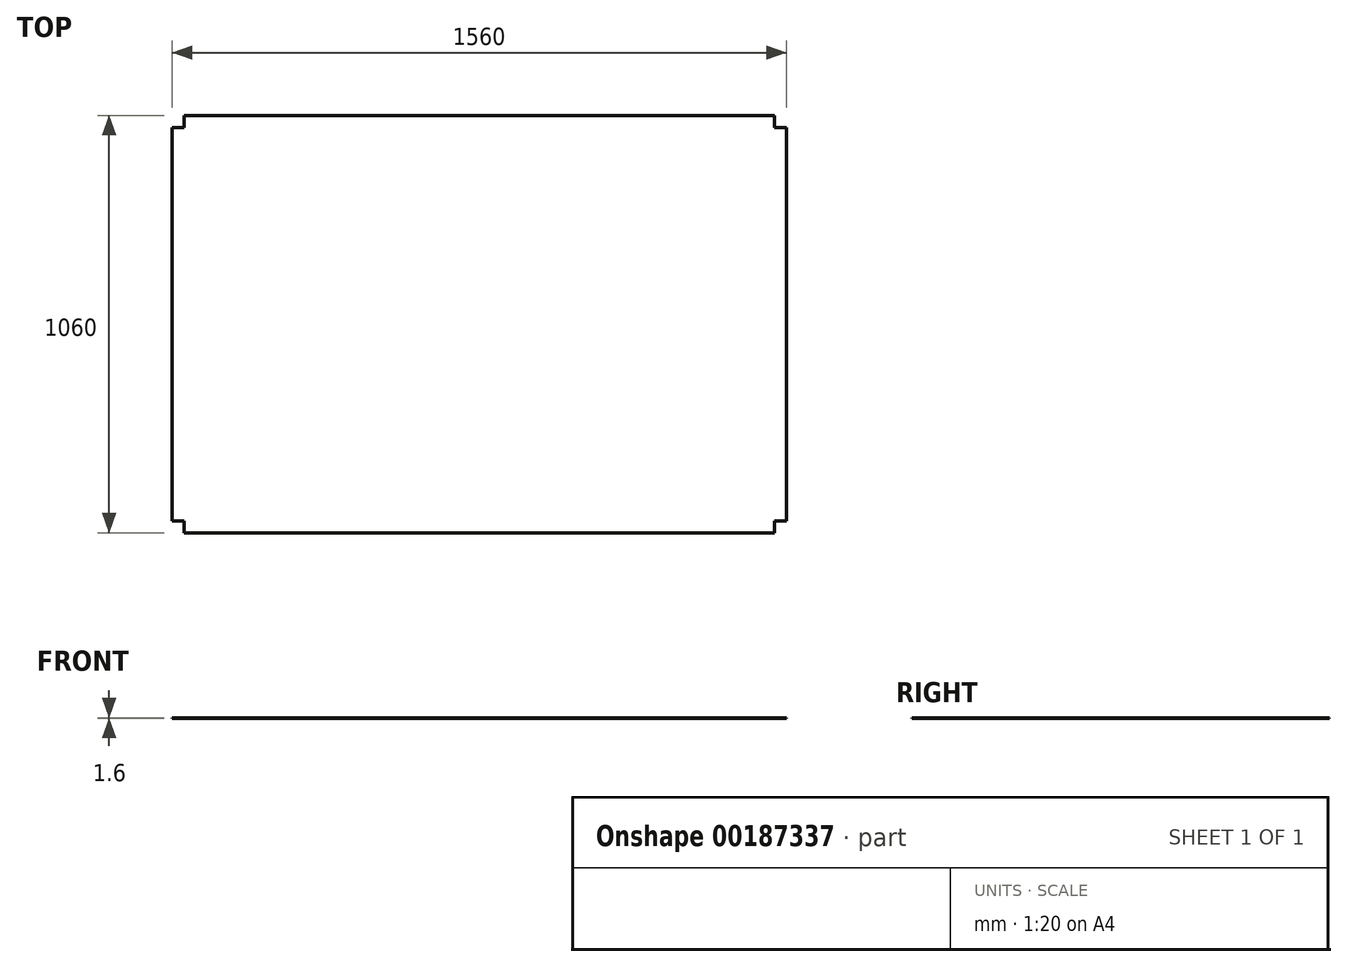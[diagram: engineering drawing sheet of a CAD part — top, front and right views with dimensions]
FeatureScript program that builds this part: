
annotation { "Feature Type Name" : "Feature", "Feature Type Description" : "" }
export const myFeature = defineFeature(function(context is Context, id is Id, definition is map)
    precondition{}
    {
        {
            var Q0;
            Q0=qCreatedBy(makeId("Top.planeOp"),FACE);
            var sketch = newSketch(context, id + "F0", { "sketchPlane" : qUnion([Q0])});
            skLineSegment(sketch, "E0.bottom", {"start": v(750, -500) * mm, "end": v(-750, -500) * mm});
            skLineSegment(sketch, "E0.top", {"start": v(750, 500) * mm, "end": v(-750, 500) * mm});
            skLineSegment(sketch, "E0.left", {"start": v(750, -500) * mm, "end": v(750, 500) * mm});
            skLineSegment(sketch, "E0.right", {"start": v(-750, -500) * mm, "end": v(-750, 500) * mm});
            skPoint(sketch, "E0.middle", {"position": v(0, 0) * mm});
            skLineSegment(sketch, "E1.0", {"start": v(750, 530) * mm, "end": v(-750, 530) * mm});
            skLineSegment(sketch, "E2.0", {"start": v(750, -530) * mm, "end": v(-750, -530) * mm});
            skLineSegment(sketch, "E3.0", {"start": v(-780, -500) * mm, "end": v(-780, 500) * mm});
            skLineSegment(sketch, "E4.0", {"start": v(780, -500) * mm, "end": v(780, 500) * mm});
            skLineSegment(sketch, "E5", {"start": v(750, 530) * mm, "end": v(750, 500) * mm});
            skLineSegment(sketch, "E6", {"start": v(780, 500) * mm, "end": v(750, 500) * mm});
            skLineSegment(sketch, "E7", {"start": v(780, -500) * mm, "end": v(750, -500) * mm});
            skLineSegment(sketch, "E8", {"start": v(750, -500) * mm, "end": v(750, -530) * mm});
            skLineSegment(sketch, "E9", {"start": v(-750, -530) * mm, "end": v(-750, -500) * mm});
            skLineSegment(sketch, "E10", {"start": v(-750, -500) * mm, "end": v(-780, -500) * mm});
            skLineSegment(sketch, "E11", {"start": v(-750, 530) * mm, "end": v(-750, 500) * mm});
            skLineSegment(sketch, "E12", {"start": v(-750, 500) * mm, "end": v(-780, 500) * mm});
            skSolve(sketch);
        }
        {
            var Q0;
            Q0=qSketchRegion(id+"F0",true);
            extrude(context, id + "F1", {"entities" : qUnion([Q0]), "depth" : 1.6 * mm});
        }
    });
